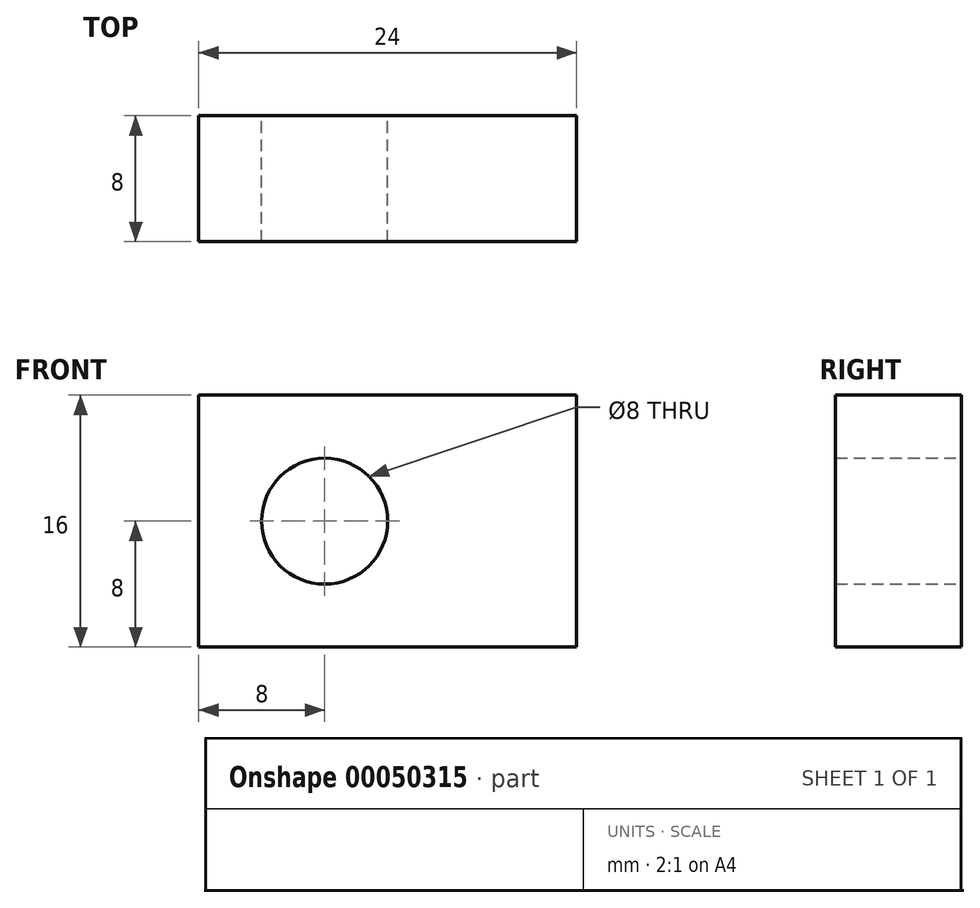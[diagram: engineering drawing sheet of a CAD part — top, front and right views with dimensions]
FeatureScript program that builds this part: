
annotation { "Feature Type Name" : "Feature", "Feature Type Description" : "" }
export const myFeature = defineFeature(function(context is Context, id is Id, definition is map)
    precondition{}
    {
        {
            var Q0;
            Q0=qCreatedBy(makeId("Front.planeOp"),FACE);
            var sketch = newSketch(context, id + "F0", { "sketchPlane" : qUnion([Q0])});
            skLineSegment(sketch, "E0.bottom", {"start": v(0, 0) * mm, "end": v(-24, 0) * mm});
            skLineSegment(sketch, "E0.top", {"start": v(0, -16) * mm, "end": v(-24, -16) * mm});
            skLineSegment(sketch, "E0.left", {"start": v(0, 0) * mm, "end": v(0, -16) * mm});
            skLineSegment(sketch, "E0.right", {"start": v(-24, 0) * mm, "end": v(-24, -16) * mm});
            skCircle(sketch, "E1", {"center": v(-16, -8) * mm, "radius": 4 * mm});
            skLineSegment(sketch, "E2", {"start": v(-8, 0) * mm, "end": v(-8, -16) * mm, "construction": true});
            skSolve(sketch);
        }
        {
            var Q0;
            Q0 = qSketchRegion(id + "F0", true);
            extrude(context, id + "F1", {"entities" : qUnion([Q0]), "depth" : 8 * mm});
        }
    });
